# Revit family: QF_WELBILT-CONVOTHERM_C-MINI-ET-10-10_3424725.240124022740
name_source: partatom
category: Specialty Equipment
units: mm (PartAtom-declared; Revit-internal decimal feet)

## family parameters
Always vertical = Yes
Cut with Voids When Loaded = No
OmniClass Number = 23.40.40.14
OmniClass Title = Food Service Equipment
Part Type = Normal
Room Calculation Point = No
Round Connector Dimension = Use Diameter
Shared = No
Work Plane-Based = No

## types (1)
- C-MINI-ET-10-10-RX_400V/3Ph/50Hz
    Accessory = No
    Apparent Power = 10500 VA
    Cold Water Flow = 0.0 L/s
    Cold Water Size = 19 mm
    Cold Water Temperature Recommended = 0 °C
    Conn Conduit = No
    Cost = 0 $
    Cycle = 50 Hz
    Default Elevation = 0 mm  [stored 0 ft]
    Depth Actual = 777 mm  [stored 2.54921 ft]
    Description = COMBI OVEN MINI EASYTOUCH 10 SHELVES GN 1/1 - RIGHT-HINGED DOOR
    Electric power = 10500 W
    FL Amps = 16 A
    Filtered Water Flow = 0.0 L/s
    Filtered Water Supply Size = 19 mm
    Height Actual = 895 mm  [stored 2.93635 ft]
    Indirect Waste Size = 38 mm
    Length Actual = 515 mm  [stored 1.68963 ft]
    Manufacturer = WELBILT-CONVOTHERM
    Max Overcurrent Protection = 0 A
    Min Ckt Ampacity = 0 A
    Model = C-MINI-ET-10-10
    Number of Poles = 1
    Phase = 3
    URL = www.convotherm.com
    Volts = 400 V
    Weight = 70.00 kg

note: [stored X ft] marks values corroborated as IEEE doubles in the binary element streams (Revit-internal decimal feet)

## geometry (parser evidence)
native form markers: Sweep x11
no freeform markers — native parametric forms only
